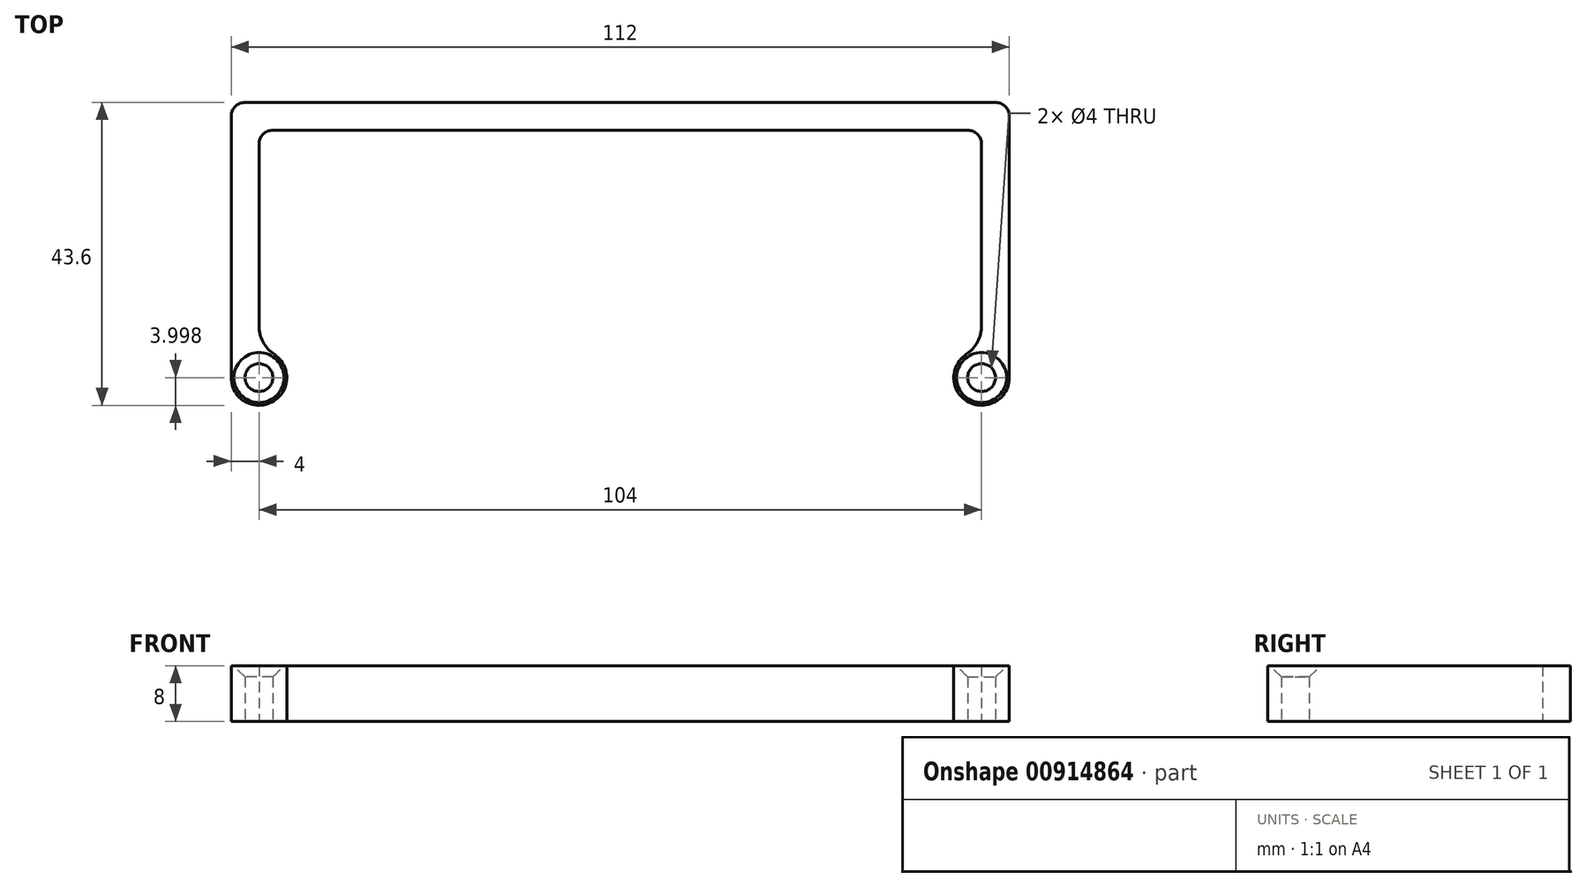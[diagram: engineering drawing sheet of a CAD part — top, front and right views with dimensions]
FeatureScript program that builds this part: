
annotation { "Feature Type Name" : "Feature", "Feature Type Description" : "" }
export const myFeature = defineFeature(function(context is Context, id is Id, definition is map)
    precondition{}
    {
        {
            var Q0;
            Q0=qCreatedBy(makeId("Top.planeOp"),FACE);
            var sketch = newSketch(context, id + "F0", { "sketchPlane" : qUnion([Q0])});
            skLineSegment(sketch, "E0", {"start": v(0, 29.69) * mm, "end": v(-52, 29.69) * mm});
            skLineSegment(sketch, "E1", {"start": v(-52, 29.69) * mm, "end": v(-52, -5.91) * mm});
            skLineSegment(sketch, "E2", {"start": v(-52, -5.91) * mm, "end": v(-56, -5.91) * mm});
            skLineSegment(sketch, "E3", {"start": v(0, 29.69) * mm, "end": v(0, 33.69) * mm});
            skLineSegment(sketch, "E4.0", {"start": v(-56, 33.69) * mm, "end": v(-56, -5.91) * mm});
            skLineSegment(sketch, "E4.1", {"start": v(0, 33.69) * mm, "end": v(-56, 33.69) * mm});
            skCircle(sketch, "E5", {"center": v(-52, -5.91) * mm, "radius": 4 * mm});
            skCircle(sketch, "E6", {"center": v(-52, -5.91) * mm, "radius": 2 * mm});
            skSolve(sketch);
        }
        {
            var Q0;
            {var subQ2=sQuery(id+"F0.wireOp",EDGE,"E0");Q0=makeQuery(id+"F0.imprint","IMPRINT",FACE,{"disambiguationData":[TD([[makeQuery(id+"F0.imprint","IMPRINT",EDGE,{"derivedFrom":subQ2}),-1.0]])]});}
            var Q1;
            {var subQ0=sQuery(id+"F0.wireOp",EDGE,"E5");var subQ1=sQuery(id+"F0.wireOp",EDGE,"E1");var subQ2=makeQuery(id+"F0.imprint","INTERSECT",VERTEX,{"derivedFrom":[subQ1,subQ0]});Q1=makeQuery(id+"F0.imprint","IMPRINT",FACE,{"disambiguationData":[TD([[makeQuery(id+"F0.imprint","IMPRINT",EDGE,{"disambiguationData":[TD([[subQ2,-1.0]])],"derivedFrom":subQ1}),-1.0]])]});}
            var Q2;
            {var subQ0=sQuery(id+"F0.wireOp",EDGE,"E5");var subQ1=sQuery(id+"F0.wireOp",EDGE,"E1");var subQ2=makeQuery(id+"F0.imprint","INTERSECT",VERTEX,{"derivedFrom":[subQ1,subQ0]});Q2=makeQuery(id+"F0.imprint","IMPRINT",FACE,{"disambiguationData":[TD([[makeQuery(id+"F0.imprint","IMPRINT",EDGE,{"disambiguationData":[TD([[subQ2,-1.0]])],"derivedFrom":subQ1}),1.0]])]});}
            extrude(context, id + "F1", {"entities" : qUnion([Q0, Q1, Q2]), "depth" : 8 * mm, "offsetDistance" : 25 * mm});
        }
        {
            var Q0;
            Q0=makeQuery(id+"F1.opExtrude","SWEPT_EDGE",EDGE,{"disambiguationData":[OSD([sQuery(id+"F0.wireOp",EDGE,"E1"),sQuery(id+"F0.wireOp",EDGE,"E5")])]});
            fillet(context, id + "F2", {"entities" : qUnion([Q0]), "radius" : 5 * mm, "tangentPropagation" : true, "allowEdgeOverflow" : false});
        }
        {
            var Q0;
            Q0=makeQuery(id+"F1.opExtrude","SWEPT_EDGE",EDGE,{"disambiguationData":[OSD([sQuery(id+"F0.wireOp",EDGE,"E0"),sQuery(id+"F0.wireOp",EDGE,"E1")])]});
            var Q1;
            Q1=makeQuery(id+"F1.opExtrude","SWEPT_EDGE",EDGE,{"disambiguationData":[OSD([sQuery(id+"F0.wireOp",EDGE,"E4.0"),sQuery(id+"F0.wireOp",EDGE,"E4.1")])]});
            fillet(context, id + "F3", {"entities" : qUnion([Q0, Q1]), "radius" : 2 * mm, "tangentPropagation" : true, "allowEdgeOverflow" : false});
        }
        {
            var Q0;
            Q0=makeQuery(id+"F1.opExtrude","CAP_EDGE",EDGE,{"disambiguationData":[OSD([sQuery(id+"F0.wireOp",EDGE,"E6")])],"isStart":false});
            chamfer(context, id + "F4", {"entities" : qUnion([Q0]), "width" : 1.6 * mm, "tangentPropagation" : true});
        }
        {
            var Q0;
            Q0=makeQuery(id+"F1.opExtrude","SWEPT_BODY",BODY,{"disambiguationData":[OSD([sQuery(id+"F0.wireOp",EDGE,"E0"),sQuery(id+"F0.wireOp",EDGE,"E1"),sQuery(id+"F0.wireOp",EDGE,"E3"),sQuery(id+"F0.wireOp",EDGE,"E4.0"),sQuery(id+"F0.wireOp",EDGE,"E4.1"),sQuery(id+"F0.wireOp",EDGE,"qWi4ZubT-rASO-Ps00-QrKg-U5esm2aCFNoB"),sQuery(id+"F0.wireOp",EDGE,"otewRyFE-N2Jv-bu2q-O1Ot-0tfRsCTFzzz8")])]});
            var Q1;
            Q1=qCreatedBy(makeId("Right.planeOp"),FACE);
            mirror(context, id + "F5", {"operationType" : NewBodyOperationType.ADD, "entities" : qUnion([Q0]), "mirrorPlane" : qUnion([Q1])});
        }
    });
